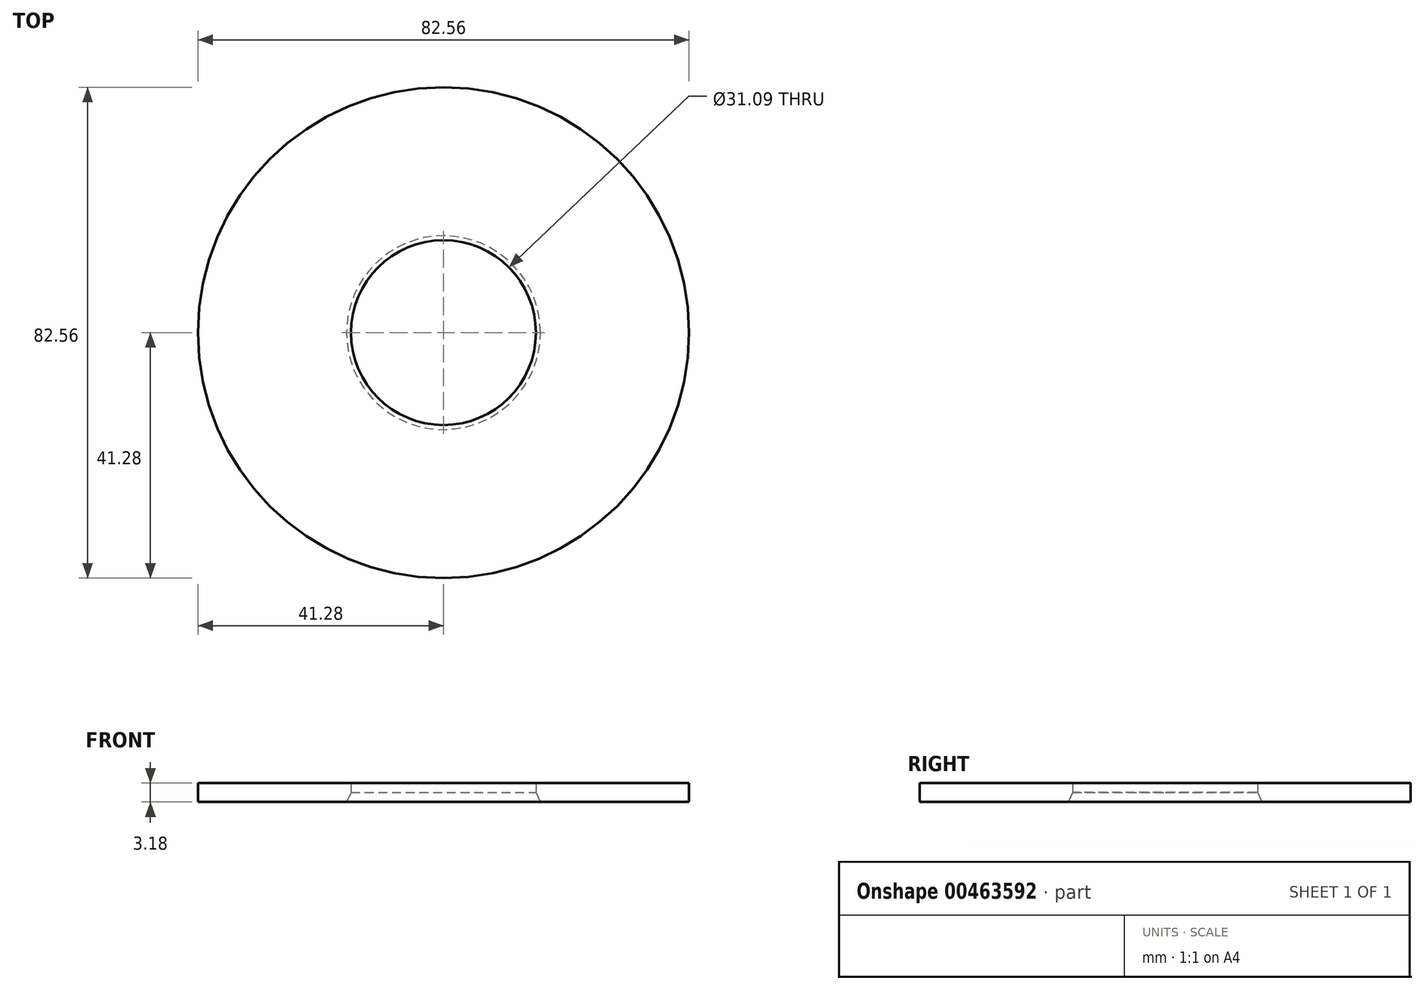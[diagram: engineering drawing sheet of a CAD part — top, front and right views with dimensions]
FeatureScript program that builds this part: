
annotation { "Feature Type Name" : "Feature", "Feature Type Description" : "" }
export const myFeature = defineFeature(function(context is Context, id is Id, definition is map)
    precondition{}
    {
        {
            var Q0;
            Q0=qCreatedBy(makeId("Front.planeOp"),FACE);
            var sketch = newSketch(context, id + "F0", { "sketchPlane" : qUnion([Q0])});
            skLineSegment(sketch, "E0", {"start": v(41.28, 3.18) * mm, "end": v(41.28, 0) * mm});
            skLineSegment(sketch, "E1", {"start": v(16.3, 0) * mm, "end": v(41.28, 0) * mm});
            skLineSegment(sketch, "E2.trimOffspring", {"start": v(15.54, 3.18) * mm, "end": v(41.28, 3.18) * mm});
            skPoint(sketch, "E3.end.orphan", {"position": v(0, 3.18) * mm});
            skLineSegment(sketch, "E4", {"start": v(0, 0) * mm, "end": v(0, 6.96) * mm, "construction": true});
            skLineSegment(sketch, "E5", {"start": v(15.54, 3.18) * mm, "end": v(15.54, 1.59) * mm});
            skLineSegment(sketch, "E6", {"start": v(15.54, 1.59) * mm, "end": v(16.3, 0) * mm});
            skSolve(sketch);
        }
        {
            var Q0;
            Q0=makeQuery(id+"F0.imprint","IMPRINT",FACE,{"disambiguationData":[TD([[makeQuery(id+"F0.imprint","IMPRINT",EDGE,{"derivedFrom":sQuery(id+"F0.wireOp",EDGE,"E0")}),-1.0]])]});
            var Q1;
            Q1=sQuery(id+"F0.wireOp",EDGE,"E4");
            revolve(context, id + "F1", {"entities" : qUnion([Q0]), "axis" : qUnion([Q1]), "revolveType" : RevolveType.FULL});
        }
    });
